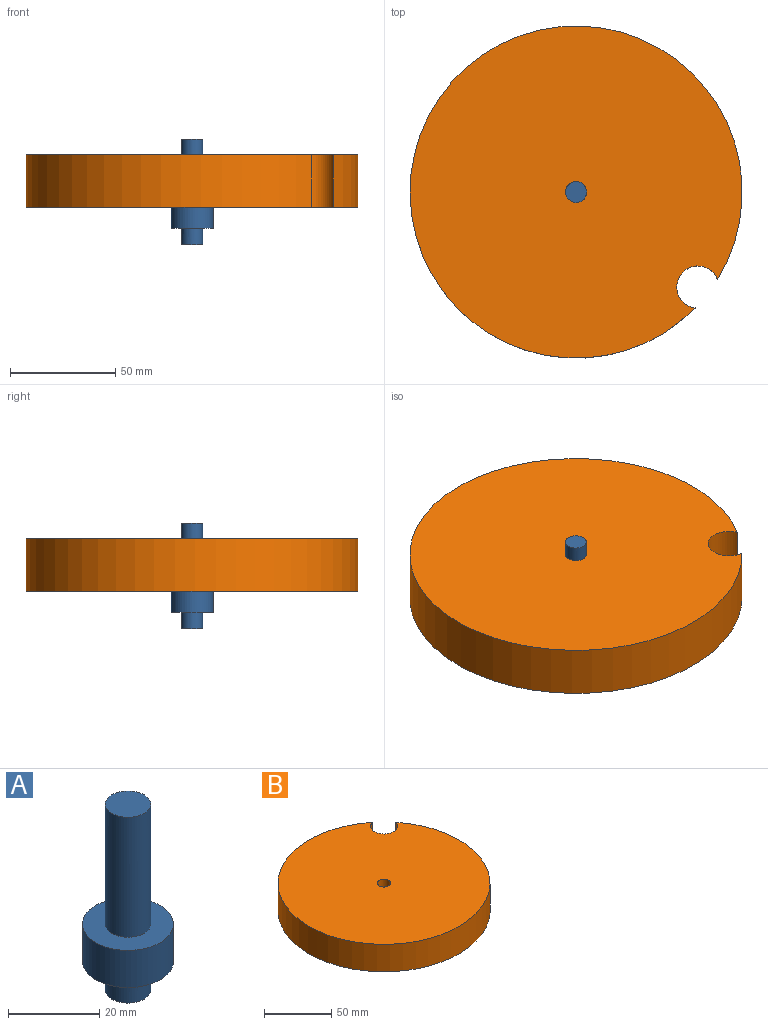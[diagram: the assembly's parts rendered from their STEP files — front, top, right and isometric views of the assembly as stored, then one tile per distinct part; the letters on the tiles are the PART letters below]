
ASSEMBLY  parts=2 mates=1
PART A: 7 faces, bbox 20x20x50 mm
  f0: cylinder r=5mm len=32.3mm, axis (0,0,-1), area 1014.6mm2, adj f1,f2
  f1: plane 10x10mm, normal (0,0,1), area 78.5mm2, adj f0
  f2: plane 20x20mm, normal (0,0,1), area 235.6mm2, adj f0,f4
  f3: plane 20x20mm, normal (0,0,-1), area 235.6mm2, adj f4,f6
  f4: cylinder r=10mm len=20mm, axis (0,0,-1), area 628.3mm2, adj f2,f3
  f5: plane 10x10mm, normal (0,0,-1), area 78.5mm2, adj f6
  f6: cylinder r=5mm len=10mm, axis (0,0,-1), area 242mm2, adj f3,f5
PART B: 5 faces, bbox 157.6x157.6x25 mm
  f0: cylinder r=78.81mm len=157.62mm, axis (0,0,-1), area 11947.8mm2, adj f2,f3,f4
  f1: cylinder r=5mm len=25mm, axis (0,0,-1), area 785.4mm2, adj f2,f3
  f2: plane 157.62x157.62mm, normal (0,0,1), area 19173.5mm2, adj f0,f1,f4
  f3: plane 157.62x157.62mm, normal (0,0,-1), area 19173.5mm2, adj f0,f1,f4
  f4: cylinder r=10mm len=25mm, axis (0,0,-1), area 1052.1mm2, adj f0,f2,f3
PLACE A at identity fixed
PLACE B rot(axis=(0,0,-1),82.9deg) t=(0,0,-7.3)mm
MATE revolute B.f1 <-> A.f0  axis (0,0,-1) through (0,0,-7.3)mm
